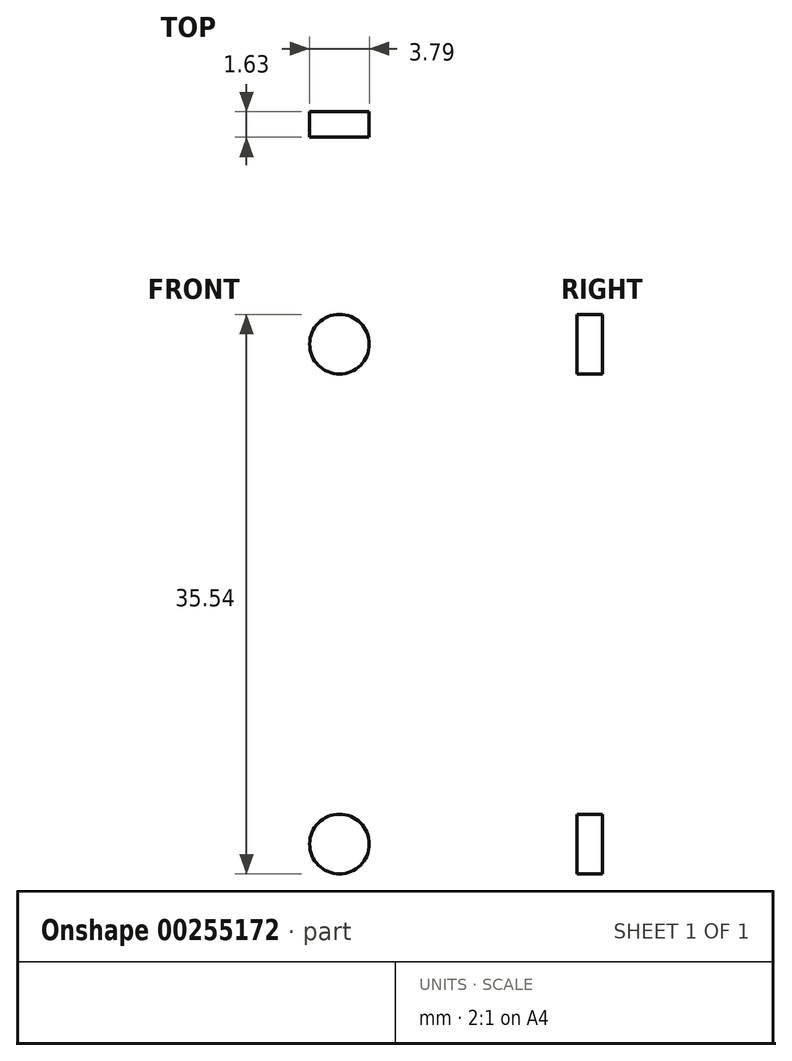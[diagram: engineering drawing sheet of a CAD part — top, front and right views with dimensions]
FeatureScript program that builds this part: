
annotation { "Feature Type Name" : "Feature", "Feature Type Description" : "" }
export const myFeature = defineFeature(function(context is Context, id is Id, definition is map)
    precondition{}
    {
        {
            var Q0;
            Q0=qCreatedBy(makeId("Front.planeOp"),FACE);
            var sketch = newSketch(context, id + "F0", { "sketchPlane" : qUnion([Q0])});
            skLineSegment(sketch, "E0.bottom", {"start": v(5.54, 55.04) * mm, "end": v(170.43, 55.04) * mm});
            skLineSegment(sketch, "E0.top", {"start": v(5.54, 0) * mm, "end": v(170.43, 0) * mm});
            skLineSegment(sketch, "E0.left", {"start": v(175.97, 49.5) * mm, "end": v(175.97, 5.54) * mm});
            skLineSegment(sketch, "E0.right", {"start": v(0, 49.5) * mm, "end": v(0, 5.54) * mm});
            skPoint(sketch, "E1.visualSharp", {"position": v(0, 55.04) * mm});
            skArc(sketch, "E1.filletArc", {"start": v(5.54, 55.04) * mm, "mid": v(1.62, 53.42) * mm, "end": v(0, 49.5) * mm});
            skPoint(sketch, "E2.visualSharp", {"position": v(175.97, 55.04) * mm});
            skArc(sketch, "E2.filletArc", {"start": v(175.97, 49.5) * mm, "mid": v(174.35, 53.42) * mm, "end": v(170.43, 55.04) * mm});
            skPoint(sketch, "E3.visualSharp", {"position": v(175.97, 0) * mm});
            skArc(sketch, "E3.filletArc", {"start": v(170.43, 0) * mm, "mid": v(174.35, 1.62) * mm, "end": v(175.97, 5.54) * mm});
            skPoint(sketch, "E4.visualSharp", {"position": v(0, 0) * mm});
            skArc(sketch, "E4.filletArc", {"start": v(0, 5.54) * mm, "mid": v(1.62, 1.62) * mm, "end": v(5.54, 0) * mm});
            skSolve(sketch);
        }
        {
            var Q0;
            Q0=qSketchRegion(id+"F0",true);
            extrude(context, id + "F1", {"entities" : qUnion([Q0]), "depth" : 1.63 * mm});
        }
        {
            var Q0;
            Q0=makeQuery(id+"F1.opExtrude","CAP_FACE",FACE,{"disambiguationData":[OSD([sQuery(id+"F0.wireOp",EDGE,"E0.bottom"),sQuery(id+"F0.wireOp",EDGE,"E0.top"),sQuery(id+"F0.wireOp",EDGE,"E0.left"),sQuery(id+"F0.wireOp",EDGE,"E0.right"),sQuery(id+"F0.wireOp",EDGE,"E1.filletArc"),sQuery(id+"F0.wireOp",EDGE,"E2.filletArc"),sQuery(id+"F0.wireOp",EDGE,"E3.filletArc"),sQuery(id+"F0.wireOp",EDGE,"E4.filletArc")])],"isStart":false});
            var sketch = newSketch(context, id + "F2", { "sketchPlane" : qUnion([Q0])});
            skCircle(sketch, "E5", {"center": v(7.37, 43.4) * mm, "radius": 1.9 * mm});
            skCircle(sketch, "E6", {"center": v(7.37, 11.65) * mm, "radius": 1.9 * mm});
            skLineSegment(sketch, "E7", {"start": v(87.99, 55.04) * mm, "end": v(87.99, 0) * mm, "construction": true});
            skCircle(sketch, "E8.MirrorC", {"center": v(168.6, 11.65) * mm, "radius": 1.9 * mm});
            skCircle(sketch, "E9.MirrorC", {"center": v(168.6, 43.4) * mm, "radius": 1.9 * mm});
            skSolve(sketch);
        }
        {
            var Q0;
            Q0=makeQuery(id+"F2.imprint","IMPRINT",FACE,{"disambiguationData":[TD([[makeQuery(id+"F2.imprint","IMPRINT",EDGE,{"derivedFrom":sQuery(id+"F2.wireOp",EDGE,"E5")}),1.0]])]});
            var Q1;
            Q1=makeQuery(id+"F2.imprint","IMPRINT",FACE,{"disambiguationData":[TD([[makeQuery(id+"F2.imprint","IMPRINT",EDGE,{"derivedFrom":sQuery(id+"F2.wireOp",EDGE,"E6")}),1.0]])]});
            var Q2;
            Q2=makeQuery(id+"F2.imprint","IMPRINT",FACE,{"disambiguationData":[TD([[makeQuery(id+"F2.imprint","IMPRINT",EDGE,{"derivedFrom":sQuery(id+"F2.wireOp",EDGE,"E9.MirrorC")}),-1.0]])]});
            var Q3;
            Q3=makeQuery(id+"F2.imprint","IMPRINT",FACE,{"disambiguationData":[TD([[makeQuery(id+"F2.imprint","IMPRINT",EDGE,{"derivedFrom":sQuery(id+"F2.wireOp",EDGE,"E8.MirrorC")}),-1.0]])]});
            extrude(context, id + "F3", {"entities" : qUnion([Q0, Q1, Q2, Q3]), "operationType" : NewBodyOperationType.REMOVE, "endBound" : BoundingType.THROUGH_ALL, "oppositeDirection" : true, "depth" : 25.4 * mm});
        }
        {
            var Q0;
            Q0=makeQuery(id+"F1.opExtrude","CAP_FACE",FACE,{"disambiguationData":[OSD([sQuery(id+"F0.wireOp",EDGE,"E0.bottom"),sQuery(id+"F0.wireOp",EDGE,"E0.top"),sQuery(id+"F0.wireOp",EDGE,"E0.left"),sQuery(id+"F0.wireOp",EDGE,"E0.right"),sQuery(id+"F0.wireOp",EDGE,"E1.filletArc"),sQuery(id+"F0.wireOp",EDGE,"E2.filletArc"),sQuery(id+"F0.wireOp",EDGE,"E3.filletArc"),sQuery(id+"F0.wireOp",EDGE,"E4.filletArc")])],"isStart":false});
            var sketch = newSketch(context, id + "F4", { "sketchPlane" : qUnion([Q0])});
            skArc(sketch, "E10", {"start": v(29.1, 42.98) * mm, "mid": v(20.27, 40.22) * mm, "end": v(29.1, 37.46) * mm});
            skLineSegment(sketch, "E11", {"start": v(29.1, 42.98) * mm, "end": v(29.1, 37.46) * mm});
            skArc(sketch, "E12", {"start": v(29.1, 17.58) * mm, "mid": v(20.27, 14.82) * mm, "end": v(29.1, 12.06) * mm});
            skLineSegment(sketch, "E13", {"start": v(29.1, 17.58) * mm, "end": v(29.1, 12.06) * mm});
            skCircle(sketch, "E14", {"center": v(25.12, 40.22) * mm, "radius": 7.25 * mm, "construction": true});
            skCircle(sketch, "E15", {"center": v(25.12, 14.82) * mm, "radius": 7.25 * mm, "construction": true});
            skArc(sketch, "E16", {"start": v(50.06, 42.98) * mm, "mid": v(41.22, 40.22) * mm, "end": v(50.06, 37.46) * mm});
            skLineSegment(sketch, "E17", {"start": v(50.06, 42.98) * mm, "end": v(50.06, 37.46) * mm});
            skArc(sketch, "E18", {"start": v(50.06, 17.58) * mm, "mid": v(41.22, 14.82) * mm, "end": v(50.06, 12.06) * mm});
            skLineSegment(sketch, "E19", {"start": v(50.06, 17.58) * mm, "end": v(50.06, 12.06) * mm});
            skCircle(sketch, "E20", {"center": v(46.08, 40.22) * mm, "radius": 7.25 * mm, "construction": true});
            skCircle(sketch, "E21", {"center": v(46.08, 14.82) * mm, "radius": 7.25 * mm, "construction": true});
            skArc(sketch, "E22", {"start": v(71.02, 42.98) * mm, "mid": v(62.18, 40.22) * mm, "end": v(71.02, 37.46) * mm});
            skLineSegment(sketch, "E23", {"start": v(71.02, 42.98) * mm, "end": v(71.02, 37.46) * mm});
            skArc(sketch, "E24", {"start": v(71.02, 17.58) * mm, "mid": v(62.18, 14.82) * mm, "end": v(71.02, 12.06) * mm});
            skLineSegment(sketch, "E25", {"start": v(71.02, 17.58) * mm, "end": v(71.02, 12.06) * mm});
            skCircle(sketch, "E26", {"center": v(67.03, 40.22) * mm, "radius": 7.25 * mm, "construction": true});
            skCircle(sketch, "E27", {"center": v(67.03, 14.82) * mm, "radius": 7.25 * mm, "construction": true});
            skArc(sketch, "E28", {"start": v(91.97, 42.98) * mm, "mid": v(83.13, 40.22) * mm, "end": v(91.97, 37.46) * mm});
            skLineSegment(sketch, "E29", {"start": v(91.97, 42.98) * mm, "end": v(91.97, 37.46) * mm});
            skArc(sketch, "E30", {"start": v(91.97, 17.58) * mm, "mid": v(83.13, 14.82) * mm, "end": v(91.97, 12.06) * mm});
            skLineSegment(sketch, "E31", {"start": v(91.97, 17.58) * mm, "end": v(91.97, 12.06) * mm});
            skCircle(sketch, "E32", {"center": v(87.99, 40.22) * mm, "radius": 7.25 * mm, "construction": true});
            skCircle(sketch, "E33", {"center": v(87.99, 14.82) * mm, "radius": 7.25 * mm, "construction": true});
            skArc(sketch, "E34", {"start": v(112.93, 42.98) * mm, "mid": v(104.09, 40.22) * mm, "end": v(112.93, 37.46) * mm});
            skLineSegment(sketch, "E35", {"start": v(112.93, 42.98) * mm, "end": v(112.93, 37.46) * mm});
            skArc(sketch, "E36", {"start": v(112.93, 17.58) * mm, "mid": v(104.09, 14.82) * mm, "end": v(112.93, 12.06) * mm});
            skLineSegment(sketch, "E37", {"start": v(112.93, 17.58) * mm, "end": v(112.93, 12.06) * mm});
            skCircle(sketch, "E38", {"center": v(108.94, 40.22) * mm, "radius": 7.25 * mm, "construction": true});
            skCircle(sketch, "E39", {"center": v(108.94, 14.82) * mm, "radius": 7.25 * mm, "construction": true});
            skArc(sketch, "E40", {"start": v(133.88, 42.98) * mm, "mid": v(125.04, 40.22) * mm, "end": v(133.88, 37.46) * mm});
            skLineSegment(sketch, "E41", {"start": v(133.88, 42.98) * mm, "end": v(133.88, 37.46) * mm});
            skArc(sketch, "E42", {"start": v(133.88, 17.58) * mm, "mid": v(125.04, 14.82) * mm, "end": v(133.88, 12.06) * mm});
            skLineSegment(sketch, "E43", {"start": v(133.88, 17.58) * mm, "end": v(133.88, 12.06) * mm});
            skCircle(sketch, "E44", {"center": v(129.9, 40.22) * mm, "radius": 7.25 * mm, "construction": true});
            skCircle(sketch, "E45", {"center": v(129.9, 14.82) * mm, "radius": 7.25 * mm, "construction": true});
            skArc(sketch, "E46", {"start": v(154.84, 42.98) * mm, "mid": v(146, 40.22) * mm, "end": v(154.84, 37.46) * mm});
            skLineSegment(sketch, "E47", {"start": v(154.84, 42.98) * mm, "end": v(154.84, 37.46) * mm});
            skArc(sketch, "E48", {"start": v(154.84, 17.58) * mm, "mid": v(146, 14.82) * mm, "end": v(154.84, 12.06) * mm});
            skLineSegment(sketch, "E49", {"start": v(154.84, 17.58) * mm, "end": v(154.84, 12.06) * mm});
            skCircle(sketch, "E50", {"center": v(150.85, 40.22) * mm, "radius": 7.25 * mm, "construction": true});
            skCircle(sketch, "E51", {"center": v(150.85, 14.82) * mm, "radius": 7.25 * mm, "construction": true});
            skSolve(sketch);
        }
        {
            var Q0;
            Q0=qSketchRegion(id+"F4",true);
            extrude(context, id + "F5", {"entities" : qUnion([Q0]), "operationType" : NewBodyOperationType.REMOVE, "endBound" : BoundingType.THROUGH_ALL, "oppositeDirection" : true, "depth" : 25.4 * mm});
        }
        {
            var Q0;
            Q0=makeQuery(id+"F1.opExtrude","CAP_FACE",FACE,{"disambiguationData":[OSD([sQuery(id+"F0.wireOp",EDGE,"E0.bottom"),sQuery(id+"F0.wireOp",EDGE,"E0.top"),sQuery(id+"F0.wireOp",EDGE,"E0.left"),sQuery(id+"F0.wireOp",EDGE,"E0.right"),sQuery(id+"F0.wireOp",EDGE,"E1.filletArc"),sQuery(id+"F0.wireOp",EDGE,"E2.filletArc"),sQuery(id+"F0.wireOp",EDGE,"E3.filletArc"),sQuery(id+"F0.wireOp",EDGE,"E4.filletArc")])],"isStart":false});
            var sketch = newSketch(context, id + "F6", { "sketchPlane" : qUnion([Q0])});
            skText(sketch, "E52", { "text": "1", "fontName": "OpenSans-Regular.ttf"});
            skLineSegment(sketch, "E53", {"start": v(25.12, 40.22) * mm, "end": v(25.12, 32.6) * mm, "construction": true});
            skLineSegment(sketch, "E54.direction1", {"start": v(25.12, 32.6) * mm, "end": v(46.08, 32.6) * mm, "construction": true});
            skText(sketch, "E55", { "text": "2", "fontName": "OpenSans-Regular.ttf"});
            skText(sketch, "E56", { "text": "3", "fontName": "OpenSans-Regular.ttf"});
            skText(sketch, "E57", { "text": "4", "fontName": "OpenSans-Regular.ttf"});
            skText(sketch, "E58", { "text": "5", "fontName": "OpenSans-Regular.ttf"});
            skText(sketch, "E59", { "text": "6", "fontName": "OpenSans-Regular.ttf"});
            skText(sketch, "E60", { "text": "7", "fontName": "OpenSans-Regular.ttf"});
            skLineSegment(sketch, "E61.0.1.0", {"start": v(25.12, 14.82) * mm, "end": v(25.12, 7.2) * mm, "construction": true});
            skLineSegment(sketch, "E61.1.0.0", {"start": v(46.08, 40.22) * mm, "end": v(46.08, 32.6) * mm, "construction": true});
            skLineSegment(sketch, "E61.1.1.0", {"start": v(46.08, 14.82) * mm, "end": v(46.08, 7.2) * mm, "construction": true});
            skLineSegment(sketch, "E61.2.0.0", {"start": v(67.03, 40.22) * mm, "end": v(67.03, 32.6) * mm, "construction": true});
            skLineSegment(sketch, "E61.2.1.0", {"start": v(67.03, 14.82) * mm, "end": v(67.03, 7.2) * mm, "construction": true});
            skLineSegment(sketch, "E61.direction2", {"start": v(25.12, 32.6) * mm, "end": v(25.12, 7.2) * mm, "construction": true});
            skLineSegment(sketch, "E62.0.3.0", {"start": v(87.99, 40.22) * mm, "end": v(87.99, 32.6) * mm, "construction": true});
            skLineSegment(sketch, "E62.0.3.1", {"start": v(87.99, 14.82) * mm, "end": v(87.99, 7.2) * mm, "construction": true});
            skLineSegment(sketch, "E62.0.4.0", {"start": v(108.94, 40.22) * mm, "end": v(108.94, 32.6) * mm, "construction": true});
            skLineSegment(sketch, "E62.0.4.1", {"start": v(108.94, 14.82) * mm, "end": v(108.94, 7.2) * mm, "construction": true});
            skLineSegment(sketch, "E62.0.5.0", {"start": v(129.9, 40.22) * mm, "end": v(129.9, 32.6) * mm, "construction": true});
            skLineSegment(sketch, "E62.0.5.1", {"start": v(129.9, 14.82) * mm, "end": v(129.9, 7.2) * mm, "construction": true});
            skLineSegment(sketch, "E62.0.6.0", {"start": v(150.85, 40.22) * mm, "end": v(150.85, 32.6) * mm, "construction": true});
            skLineSegment(sketch, "E62.0.6.1", {"start": v(150.85, 14.82) * mm, "end": v(150.85, 7.2) * mm, "construction": true});
            skText(sketch, "E63", { "text": "8", "fontName": "OpenSans-Regular.ttf"});
            skText(sketch, "E64", { "text": "9", "fontName": "OpenSans-Regular.ttf"});
            skText(sketch, "E65", { "text": "10", "fontName": "OpenSans-Regular.ttf"});
            skText(sketch, "E66", { "text": "11", "fontName": "OpenSans-Regular.ttf"});
            skText(sketch, "E67", { "text": "12", "fontName": "OpenSans-Regular.ttf"});
            skText(sketch, "E68", { "text": "13", "fontName": "OpenSans-Regular.ttf"});
            skText(sketch, "E69", { "text": "14", "fontName": "OpenSans-Regular.ttf"});
            const initialGuessF6  = {"E52": [0.02291, 0.02752, 1, 0, 0.00508], "E55": [0.04402, 0.02752, 1, 0, 0.00508], "E56": [0.065, 0.02752, 1, 0, 0.00508], "E57": [0.08581, 0.02752, 1, 0, 0.00508], "E58": [0.1069, 0.02752, 1, 0, 0.00508], "E59": [0.12782, 0.02752, 1, 0, 0.00508], "E60": [0.14878, 0.02752, 1, 0, 0.00508], "E63": [0.02306, 0.00212, 1, 0, 0.00508], "E64": [0.04402, 0.00212, 1, 0, 0.00508], "E65": [0.06294, 0.00212, 1, 0, 0.00508], "E66": [0.0845, 0.00212, 1, 0, 0.00508], "E67": [0.10487, 0.00212, 1, 0, 0.00508], "E68": [0.12584, 0.00212, 1, 0, 0.00508], "E69": [0.14666, 0.00212, 1, 0, 0.00508]};
            skSetInitialGuess(sketch, initialGuessF6);
            skSolve(sketch);
        }
        {
            var Q0;
            Q0 = qSketchRegion(id + "F6", true);
            extrude(context, id + "F7", {"entities" : qUnion([Q0]), "operationType" : NewBodyOperationType.REMOVE, "oppositeDirection" : true, "depth" : 1.27 * mm, "offsetDistance" : 25.4 * mm});
        }
        {
            var Q0;
            Q0 = qSketchRegion(id + "F6", true);
            extrude(context, id + "F8", {"entities" : qUnion([Q0]), "operationType" : NewBodyOperationType.REMOVE, "oppositeDirection" : true, "depth" : 1.27 * mm, "offsetDistance" : 25.4 * mm});
        }
    });
